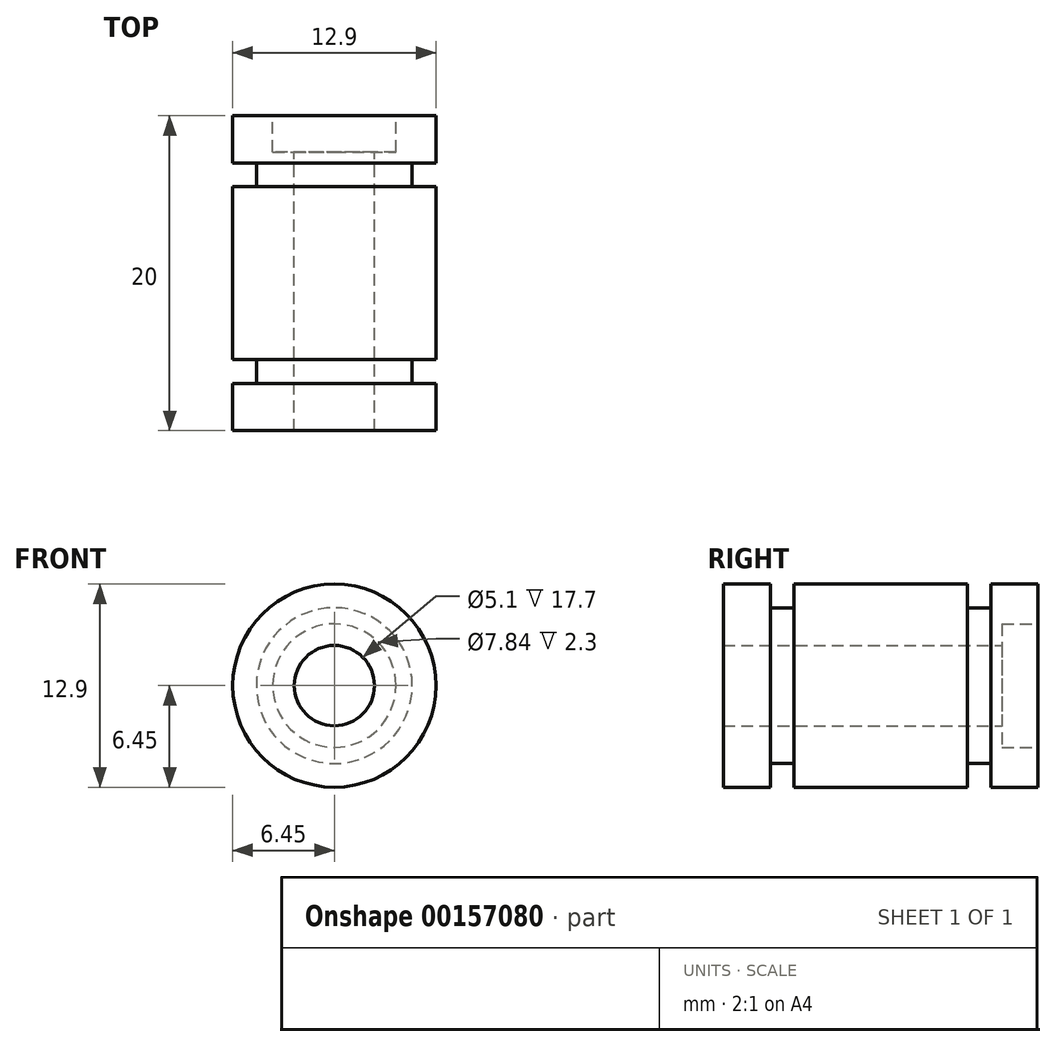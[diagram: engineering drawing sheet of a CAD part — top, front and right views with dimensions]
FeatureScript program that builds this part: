
annotation { "Feature Type Name" : "Feature", "Feature Type Description" : "" }
export const myFeature = defineFeature(function(context is Context, id is Id, definition is map)
    precondition{}
    {
        {
            var Q0;
            Q0=qCreatedBy(makeId("Right.planeOp"),FACE);
            var sketch = newSketch(context, id + "F0", { "sketchPlane" : qUnion([Q0])});
            skLineSegment(sketch, "E0", {"start": v(11.47, 0) * mm, "end": v(0, 0) * mm, "construction": true});
            skLineSegment(sketch, "E1", {"start": v(17.7, 2.55) * mm, "end": v(0, 2.55) * mm});
            skLineSegment(sketch, "E2", {"start": v(17.7, 2.55) * mm, "end": v(17.7, 3.92) * mm});
            skLineSegment(sketch, "E3", {"start": v(20, 3.92) * mm, "end": v(17.7, 3.92) * mm});
            skLineSegment(sketch, "E4", {"start": v(20, 3.92) * mm, "end": v(20, 6.45) * mm});
            skLineSegment(sketch, "E5", {"start": v(17, 6.45) * mm, "end": v(20, 6.45) * mm});
            skLineSegment(sketch, "E6", {"start": v(17, 6.45) * mm, "end": v(17, 4.95) * mm});
            skLineSegment(sketch, "E7", {"start": v(15.5, 4.95) * mm, "end": v(17, 4.95) * mm});
            skLineSegment(sketch, "E8", {"start": v(3, 4.95) * mm, "end": v(3, 6.45) * mm});
            skLineSegment(sketch, "E9", {"start": v(0, 6.45) * mm, "end": v(3, 6.45) * mm});
            skLineSegment(sketch, "E10", {"start": v(0, 6.45) * mm, "end": v(0, 2.55) * mm});
            skLineSegment(sketch, "E11", {"start": v(4.5, 4.95) * mm, "end": v(4.5, 6.45) * mm});
            skLineSegment(sketch, "E12", {"start": v(4.5, 6.45) * mm, "end": v(15.5, 6.45) * mm});
            skLineSegment(sketch, "E13", {"start": v(15.5, 6.45) * mm, "end": v(15.5, 4.95) * mm});
            skLineSegment(sketch, "E14.trimOffspring", {"start": v(4.5, 4.95) * mm, "end": v(3, 4.95) * mm});
            skSolve(sketch);
        }
        {
            var Q0;
            Q0=makeQuery(id+"F0.imprint","IMPRINT",FACE,{"disambiguationData":[TD([[makeQuery(id+"F0.imprint","IMPRINT",EDGE,{"derivedFrom":sQuery(id+"F0.wireOp",EDGE,"E1")}),-1.0]])]});
            var Q1;
            Q1=sQuery(id+"F0.wireOp",EDGE,"E0");
            revolve(context, id + "F1", {"entities" : qUnion([Q0]), "axis" : qUnion([Q1]), "revolveType" : RevolveType.FULL});
        }
    });
